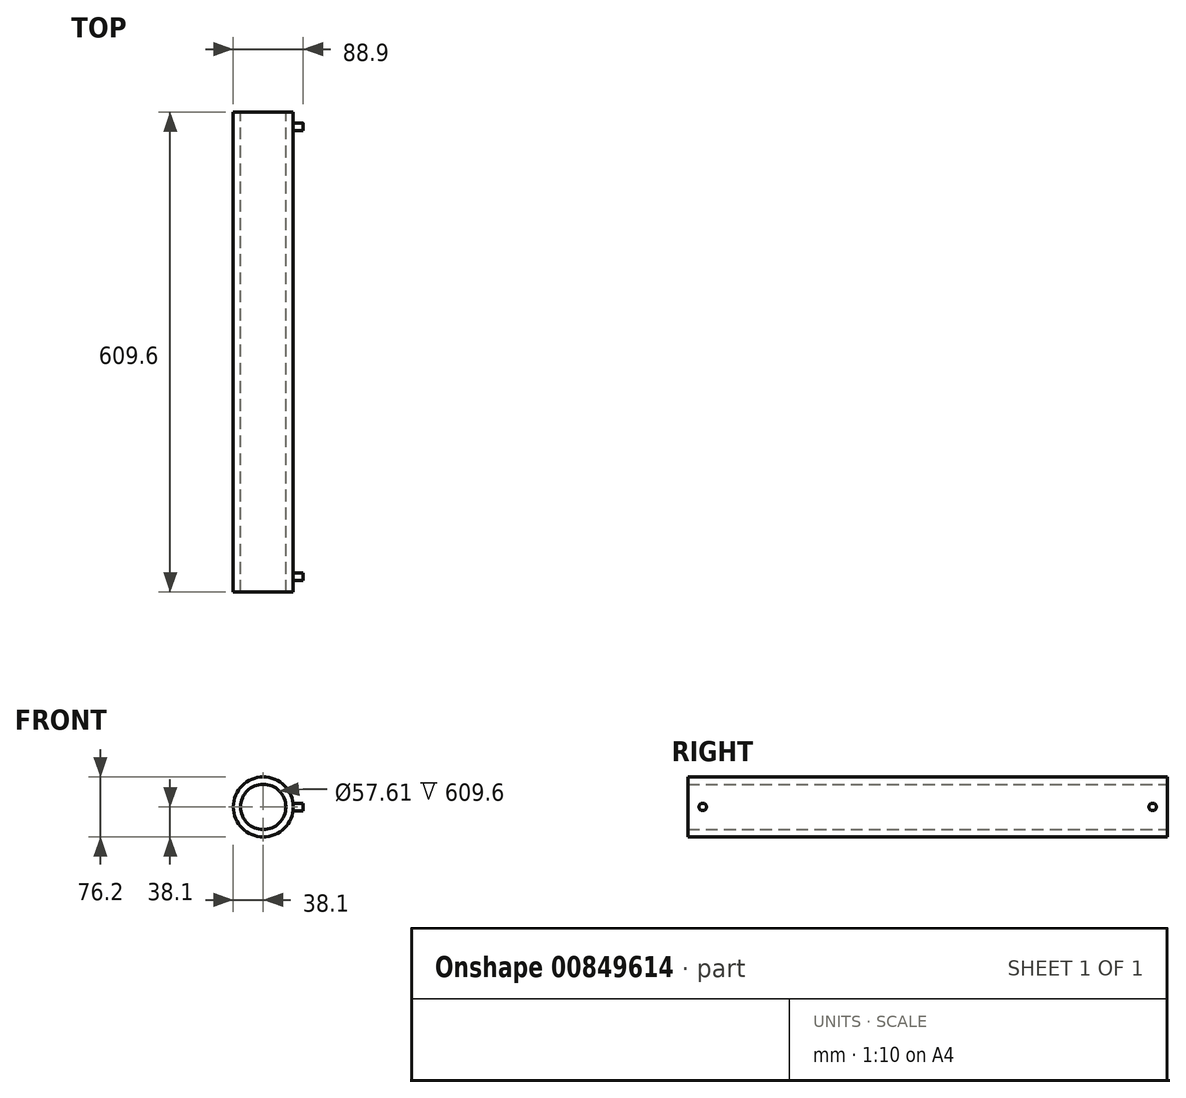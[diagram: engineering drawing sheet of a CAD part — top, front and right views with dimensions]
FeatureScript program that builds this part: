
annotation { "Feature Type Name" : "Feature", "Feature Type Description" : "" }
export const myFeature = defineFeature(function(context is Context, id is Id, definition is map)
    precondition{}
    {
        {
            var Q0;
            Q0=qCreatedBy(makeId("Front.planeOp"),FACE);
            var sketch = newSketch(context, id + "F0", { "sketchPlane" : qUnion([Q0])});
            skCircle(sketch, "E0", {"center": v(0, 0) * mm, "radius": 40.2 * mm});
            skCircle(sketch, "E1", {"center": v(0, 0) * mm, "radius": 42.75 * mm});
            skCircle(sketch, "E2", {"center": v(0, 0) * mm, "radius": 38.1 * mm});
            skCircle(sketch, "E3", {"center": v(0, 0) * mm, "radius": 28.8 * mm});
            skSolve(sketch);
        }
        {
            var Q0;
            Q0=qCreatedBy(makeId("Right.planeOp"),FACE);
            var sketch = newSketch(context, id + "F1", { "sketchPlane" : qUnion([Q0])});
            skCircle(sketch, "E4", {"center": v(-19.05, 0) * mm, "radius": 4.76 * mm});
            skCircle(sketch, "E5", {"center": v(-285.75, 0) * mm, "radius": 4.76 * mm});
            skSolve(sketch);
        }
        {
            var Q0;
            Q0=makeQuery(id+"F1.imprint","IMPRINT",FACE,{"disambiguationData":[TD([[makeQuery(id+"F1.imprint","IMPRINT",EDGE,{"derivedFrom":sQuery(id+"F1.wireOp",EDGE,"E4")}),1.0]])]});
            extrude(context, id + "F2", {"entities" : qUnion([Q0]), "depth" : 50.8 * mm, "offsetDistance" : 25.4 * mm});
        }
        {
            var Q0;
            Q0=makeQuery(id+"F0.imprint","IMPRINT",FACE,{"disambiguationData":[TD([[makeQuery(id+"F0.imprint","IMPRINT",EDGE,{"derivedFrom":sQuery(id+"F0.wireOp",EDGE,"E2")}),1.0]])]});
            var Q1;
            Q1=makeQuery(id+"F0.imprint","IMPRINT",FACE,{"disambiguationData":[TD([[makeQuery(id+"F0.imprint","IMPRINT",EDGE,{"derivedFrom":sQuery(id+"F0.wireOp",EDGE,"E3")}),1.0]])]});
            extrude(context, id + "F3", {"entities" : qUnion([Q0, Q1]), "operationType" : NewBodyOperationType.ADD, "depth" : 304.8 * mm, "offsetDistance" : 25.4 * mm});
        }
        {
            var Q0;
            Q0=makeQuery(id+"F0.imprint","IMPRINT",FACE,{"disambiguationData":[TD([[makeQuery(id+"F0.imprint","IMPRINT",EDGE,{"derivedFrom":sQuery(id+"F0.wireOp",EDGE,"E3")}),1.0]])]});
            extrude(context, id + "F4", {"entities" : qUnion([Q0]), "operationType" : NewBodyOperationType.REMOVE, "depth" : 304.8 * mm, "offsetDistance" : 25.4 * mm});
        }
        {
            var Q0;
            Q0=makeQuery(id+"F2.opExtrude","SWEPT_BODY",BODY,{"disambiguationData":[OSD([sQuery(id+"F1.wireOp",EDGE,"E4")])]});
            var Q1;
            Q1=makeQuery(id+"F3.opExtrude","CAP_FACE",FACE,{"disambiguationData":[OSD([sQuery(id+"F0.wireOp",EDGE,"E2")])],"isStart":false});
            mirror(context, id + "F5", {"operationType" : NewBodyOperationType.ADD, "entities" : qUnion([Q0]), "mirrorPlane" : qUnion([Q1])});
        }
    });
